# Revit family: Sirena electronica con foco_Aguilera Electronica
name_source: partatom
category: Dispositivos de alarma de incendios
revit_build: Autodesk Revit 2017 (Build: 20160225_1515(x64)
units: mm (PartAtom-declared; Revit-internal decimal feet)

## family parameters
Anfitrión = Cara
Compartido = No
Corte con vacíos al cargar = No
Cota de conector redondo = Diámetro de uso
Mantener orientación de anotación = Sí
Número OmniClass = 23.85.30.21.14.11
Punto de cálculo de habitación = No
Tipo de pieza = Normal
Título OmniClass = Concentration Detection Bells and Sounders

## types (1)
- Sirena electrónica con foco EN54-23
    Altura 1 = 10 mm  [stored 0.0328084 ft]
    Altura 2 = 53 mm  [stored 0.173885 ft]
    Altura 3 = 17 mm
    Altura 4 = 30 mm  [stored 0.0984252 ft]
    Comentarios de tipo = Sirena multitono con foco certificada EN 54-3 y EN 54-23 para montaje en pared. Tipo W-2.4-7.5.

Máxima altura de instalación 2.4m, longitud de cobertura 7.5 m.
Tecnología led que garantiza una intensidad luminosa 0.4lux/m2 en todo el área.
Nivel sonoro 102dB(A).
Consumo máximo 37mA.
Protección IP65.
    Descripción = La sirena AE/ASFLXW es ideal para aplicaciones de uso dual en las que
se exige un dispositivo de alarma visual además de una alarma audible.
Esta especialmente recomendado para su uso en pared ya que solo
requiere un punto de instalación. Preparada para usar con cualquier sonda
estándar.
Certificada EN-3 y EN 54-23 para montaje en pared.
    Diámetro tubo = 20 mm  [stored 0.0656168 ft]
    Elevación por defecto = 1200 mm
    Fabricante = Aguilera Electrónica
    Modelo = AE/V-ASFLXW
    Símbolo = Sí
    Símbolo texto modelo = Sí
    URL = https://aguilera.es

note: [stored X ft] marks values corroborated as IEEE doubles in the binary element streams (Revit-internal decimal feet)
